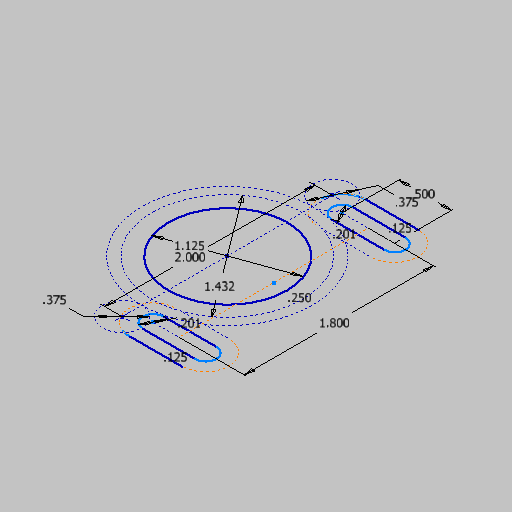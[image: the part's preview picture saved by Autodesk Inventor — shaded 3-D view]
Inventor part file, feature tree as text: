
AUTODESK INVENTOR PART (.ipt)
format: ipt  version: 2023.5 (Build 275446000, 446)  size: 134,144 bytes
history: native  units: in
note: dims shown in document units (in); Inventor stores cm internally (conversion verified against a paired STEP export)
features: sketch x2, extrude x2, plane x2, fillet x1, projected_geometry x1
ambient origin geometry x8: Origin, YZ Plane, XZ Plane, XY Plane, X Axis, Y Axis, Z Axis, Center Point
bodies: Solid1 (feature_tree)
feature tree (8):
  sketch  "Sketch1"  dims[d0=1.125in d1=2.0in]
  extrude  "Extrusion1"  Depth=2.0in
  extrude  "Extrusion2"  Depth=0.375in
  fillet  "Fillet1"  Radius=0.375in
  plane  "Work Plane1"
  plane  "Work Plane2"
  sketch  "Sketch2"  dims[d2=1.432in d3=0.375in d4=0.375in d5=0.25in d6=0.25in d7=0.0in d15=0.094in d16=0.825in d17=1.0in d18=0.0in d19=0.125in d20=0.201in d21=0.201in d22=0.5in d25=0.125in d26=0.125in d27=1.8in]
  projected_geometry  "Project Cut Edges1"
